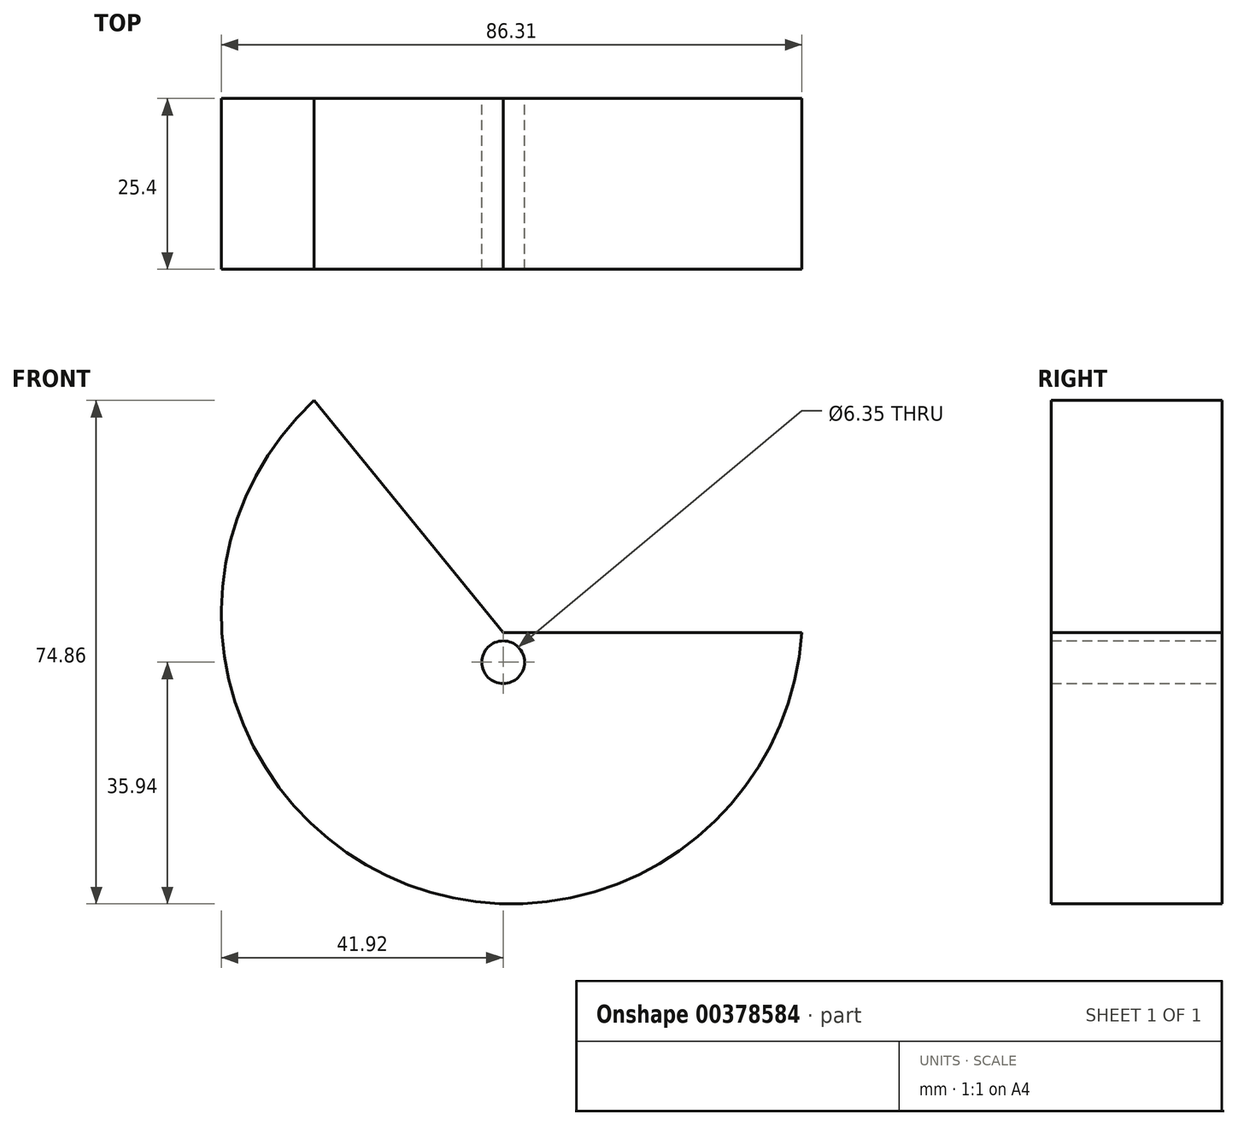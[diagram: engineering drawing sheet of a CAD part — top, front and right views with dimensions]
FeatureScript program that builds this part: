
annotation { "Feature Type Name" : "Feature", "Feature Type Description" : "" }
export const myFeature = defineFeature(function(context is Context, id is Id, definition is map)
    precondition{}
    {
        {
            var Q0;
            Q0=qCreatedBy(makeId("Front.planeOp"),FACE);
            var sketch = newSketch(context, id + "F0", { "sketchPlane" : qUnion([Q0])});
            skCircle(sketch, "E0", {"center": v(0, 0) * mm, "radius": 3.18 * mm});
            skLineSegment(sketch, "E1", {"start": v(0, 4.38) * mm, "end": v(44.39, 4.38) * mm});
            skLineSegment(sketch, "E2", {"start": v(0, 4.38) * mm, "end": v(-28.1, 38.92) * mm});
            skArc(sketch, "E3", {"start": v(-28.1, 38.92) * mm, "mid": v(-17.3, -31.74) * mm, "end": v(44.39, 4.38) * mm});
            skSolve(sketch);
        }
        {
            var Q0;
            {var subQ0=sQuery(id+"F0.wireOp",EDGE,"6a9a65d7-652e-4bca-9d3c-62b15c011ce0.27.0");var subQ1=sQuery(id+"F0.wireOp",EDGE,"dYePoZEX-iQU0-QvIu-3Huc-MhSANwJ4F8yg");var subQ2=makeQuery(id+"F0.imprint","INTERSECT",VERTEX,{"disambiguationData":[OD(0.0)],"derivedFrom":[subQ1,subQ0]});Q0=makeQuery(id+"F0.imprint","IMPRINT",FACE,{"disambiguationData":[TD([[makeQuery(id+"F0.imprint","IMPRINT",EDGE,{"disambiguationData":[TD([[subQ2,1.0]])],"derivedFrom":subQ1}),-1.0]])]});}
            var Q1;
            {var subQ0=sQuery(id+"F0.wireOp",EDGE,"6a9a65d7-652e-4bca-9d3c-62b15c011ce0.29.0");var subQ1=sQuery(id+"F0.wireOp",EDGE,"dYePoZEX-iQU0-QvIu-3Huc-MhSANwJ4F8yg");var subQ2=makeQuery(id+"F0.imprint","INTERSECT",VERTEX,{"disambiguationData":[OD(0.0)],"derivedFrom":[subQ1,subQ0]});Q1=makeQuery(id+"F0.imprint","IMPRINT",FACE,{"disambiguationData":[TD([[makeQuery(id+"F0.imprint","IMPRINT",EDGE,{"disambiguationData":[TD([[subQ2,-1.0]])],"derivedFrom":subQ1}),-1.0]])]});}
            var Q2;
            {var subQ0=sQuery(id+"F0.wireOp",EDGE,"QKdbO5Jt-CDva-Epwn-0zTl-117RtQSzYKU9");var subQ1=sQuery(id+"F0.wireOp",EDGE,"dYePoZEX-iQU0-QvIu-3Huc-MhSANwJ4F8yg");var subQ2=makeQuery(id+"F0.imprint","INTERSECT",VERTEX,{"disambiguationData":[OD(0.0)],"derivedFrom":[subQ1,subQ0]});Q2=makeQuery(id+"F0.imprint","IMPRINT",FACE,{"disambiguationData":[TD([[makeQuery(id+"F0.imprint","IMPRINT",EDGE,{"disambiguationData":[TD([[subQ2,-1.0]])],"derivedFrom":subQ1}),-1.0]])]});}
            var Q3;
            {var subQ0=sQuery(id+"F0.wireOp",EDGE,"6a9a65d7-652e-4bca-9d3c-62b15c011ce0.1.0");var subQ1=sQuery(id+"F0.wireOp",EDGE,"dYePoZEX-iQU0-QvIu-3Huc-MhSANwJ4F8yg");var subQ2=makeQuery(id+"F0.imprint","INTERSECT",VERTEX,{"disambiguationData":[OD(0.0)],"derivedFrom":[subQ1,subQ0]});Q3=makeQuery(id+"F0.imprint","IMPRINT",FACE,{"disambiguationData":[TD([[makeQuery(id+"F0.imprint","IMPRINT",EDGE,{"disambiguationData":[TD([[subQ2,-1.0]])],"derivedFrom":subQ1}),-1.0]])]});}
            var Q4;
            {var subQ0=sQuery(id+"F0.wireOp",EDGE,"6a9a65d7-652e-4bca-9d3c-62b15c011ce0.2.0");var subQ1=sQuery(id+"F0.wireOp",EDGE,"dYePoZEX-iQU0-QvIu-3Huc-MhSANwJ4F8yg");var subQ2=makeQuery(id+"F0.imprint","INTERSECT",VERTEX,{"disambiguationData":[OD(0.0)],"derivedFrom":[subQ1,subQ0]});Q4=makeQuery(id+"F0.imprint","IMPRINT",FACE,{"disambiguationData":[TD([[makeQuery(id+"F0.imprint","IMPRINT",EDGE,{"disambiguationData":[TD([[subQ2,-1.0]])],"derivedFrom":subQ1}),-1.0]])]});}
            var Q5;
            {var subQ0=sQuery(id+"F0.wireOp",EDGE,"6a9a65d7-652e-4bca-9d3c-62b15c011ce0.3.0");var subQ1=sQuery(id+"F0.wireOp",EDGE,"dYePoZEX-iQU0-QvIu-3Huc-MhSANwJ4F8yg");var subQ2=makeQuery(id+"F0.imprint","INTERSECT",VERTEX,{"disambiguationData":[OD(0.0)],"derivedFrom":[subQ1,subQ0]});Q5=makeQuery(id+"F0.imprint","IMPRINT",FACE,{"disambiguationData":[TD([[makeQuery(id+"F0.imprint","IMPRINT",EDGE,{"disambiguationData":[TD([[subQ2,-1.0]])],"derivedFrom":subQ1}),-1.0]])]});}
            var Q6;
            {var subQ0=sQuery(id+"F0.wireOp",EDGE,"6a9a65d7-652e-4bca-9d3c-62b15c011ce0.4.0");var subQ1=sQuery(id+"F0.wireOp",EDGE,"dYePoZEX-iQU0-QvIu-3Huc-MhSANwJ4F8yg");var subQ2=makeQuery(id+"F0.imprint","INTERSECT",VERTEX,{"disambiguationData":[OD(0.0)],"derivedFrom":[subQ1,subQ0]});Q6=makeQuery(id+"F0.imprint","IMPRINT",FACE,{"disambiguationData":[TD([[makeQuery(id+"F0.imprint","IMPRINT",EDGE,{"disambiguationData":[TD([[subQ2,-1.0]])],"derivedFrom":subQ1}),-1.0]])]});}
            var Q7;
            {var subQ0=sQuery(id+"F0.wireOp",EDGE,"6a9a65d7-652e-4bca-9d3c-62b15c011ce0.5.0");var subQ1=sQuery(id+"F0.wireOp",EDGE,"dYePoZEX-iQU0-QvIu-3Huc-MhSANwJ4F8yg");var subQ2=makeQuery(id+"F0.imprint","INTERSECT",VERTEX,{"disambiguationData":[OD(0.0)],"derivedFrom":[subQ1,subQ0]});Q7=makeQuery(id+"F0.imprint","IMPRINT",FACE,{"disambiguationData":[TD([[makeQuery(id+"F0.imprint","IMPRINT",EDGE,{"disambiguationData":[TD([[subQ2,-1.0]])],"derivedFrom":subQ1}),-1.0]])]});}
            var Q8;
            {var subQ0=sQuery(id+"F0.wireOp",EDGE,"6a9a65d7-652e-4bca-9d3c-62b15c011ce0.6.0");var subQ1=sQuery(id+"F0.wireOp",EDGE,"dYePoZEX-iQU0-QvIu-3Huc-MhSANwJ4F8yg");var subQ2=makeQuery(id+"F0.imprint","INTERSECT",VERTEX,{"disambiguationData":[OD(0.0)],"derivedFrom":[subQ1,subQ0]});Q8=makeQuery(id+"F0.imprint","IMPRINT",FACE,{"disambiguationData":[TD([[makeQuery(id+"F0.imprint","IMPRINT",EDGE,{"disambiguationData":[TD([[subQ2,-1.0]])],"derivedFrom":subQ1}),-1.0]])]});}
            var Q9;
            {var subQ0=sQuery(id+"F0.wireOp",EDGE,"6a9a65d7-652e-4bca-9d3c-62b15c011ce0.7.0");var subQ1=sQuery(id+"F0.wireOp",EDGE,"dYePoZEX-iQU0-QvIu-3Huc-MhSANwJ4F8yg");var subQ2=makeQuery(id+"F0.imprint","INTERSECT",VERTEX,{"disambiguationData":[OD(0.0)],"derivedFrom":[subQ1,subQ0]});Q9=makeQuery(id+"F0.imprint","IMPRINT",FACE,{"disambiguationData":[TD([[makeQuery(id+"F0.imprint","IMPRINT",EDGE,{"disambiguationData":[TD([[subQ2,-1.0]])],"derivedFrom":subQ1}),-1.0]])]});}
            var Q10;
            {var subQ0=sQuery(id+"F0.wireOp",EDGE,"6a9a65d7-652e-4bca-9d3c-62b15c011ce0.8.0");var subQ1=sQuery(id+"F0.wireOp",EDGE,"dYePoZEX-iQU0-QvIu-3Huc-MhSANwJ4F8yg");var subQ2=makeQuery(id+"F0.imprint","INTERSECT",VERTEX,{"disambiguationData":[OD(0.0)],"derivedFrom":[subQ1,subQ0]});Q10=makeQuery(id+"F0.imprint","IMPRINT",FACE,{"disambiguationData":[TD([[makeQuery(id+"F0.imprint","IMPRINT",EDGE,{"disambiguationData":[TD([[subQ2,-1.0]])],"derivedFrom":subQ1}),-1.0]])]});}
            var Q11;
            {var subQ0=sQuery(id+"F0.wireOp",EDGE,"6a9a65d7-652e-4bca-9d3c-62b15c011ce0.9.0");var subQ1=sQuery(id+"F0.wireOp",EDGE,"dYePoZEX-iQU0-QvIu-3Huc-MhSANwJ4F8yg");var subQ2=makeQuery(id+"F0.imprint","INTERSECT",VERTEX,{"disambiguationData":[OD(0.0)],"derivedFrom":[subQ1,subQ0]});Q11=makeQuery(id+"F0.imprint","IMPRINT",FACE,{"disambiguationData":[TD([[makeQuery(id+"F0.imprint","IMPRINT",EDGE,{"disambiguationData":[TD([[subQ2,-1.0]])],"derivedFrom":subQ1}),-1.0]])]});}
            var Q12;
            {var subQ0=sQuery(id+"F0.wireOp",EDGE,"6a9a65d7-652e-4bca-9d3c-62b15c011ce0.10.0");var subQ1=sQuery(id+"F0.wireOp",EDGE,"dYePoZEX-iQU0-QvIu-3Huc-MhSANwJ4F8yg");var subQ2=makeQuery(id+"F0.imprint","INTERSECT",VERTEX,{"disambiguationData":[OD(0.0)],"derivedFrom":[subQ1,subQ0]});Q12=makeQuery(id+"F0.imprint","IMPRINT",FACE,{"disambiguationData":[TD([[makeQuery(id+"F0.imprint","IMPRINT",EDGE,{"disambiguationData":[TD([[subQ2,-1.0]])],"derivedFrom":subQ1}),-1.0]])]});}
            var Q13;
            {var subQ0=sQuery(id+"F0.wireOp",EDGE,"6a9a65d7-652e-4bca-9d3c-62b15c011ce0.11.0");var subQ1=sQuery(id+"F0.wireOp",EDGE,"dYePoZEX-iQU0-QvIu-3Huc-MhSANwJ4F8yg");var subQ2=makeQuery(id+"F0.imprint","INTERSECT",VERTEX,{"disambiguationData":[OD(0.0)],"derivedFrom":[subQ1,subQ0]});Q13=makeQuery(id+"F0.imprint","IMPRINT",FACE,{"disambiguationData":[TD([[makeQuery(id+"F0.imprint","IMPRINT",EDGE,{"disambiguationData":[TD([[subQ2,-1.0]])],"derivedFrom":subQ1}),-1.0]])]});}
            var Q14;
            {var subQ0=sQuery(id+"F0.wireOp",EDGE,"6a9a65d7-652e-4bca-9d3c-62b15c011ce0.12.0");var subQ1=sQuery(id+"F0.wireOp",EDGE,"dYePoZEX-iQU0-QvIu-3Huc-MhSANwJ4F8yg");var subQ2=makeQuery(id+"F0.imprint","INTERSECT",VERTEX,{"disambiguationData":[OD(0.0)],"derivedFrom":[subQ1,subQ0]});Q14=makeQuery(id+"F0.imprint","IMPRINT",FACE,{"disambiguationData":[TD([[makeQuery(id+"F0.imprint","IMPRINT",EDGE,{"disambiguationData":[TD([[subQ2,-1.0]])],"derivedFrom":subQ1}),-1.0]])]});}
            var Q15;
            {var subQ0=sQuery(id+"F0.wireOp",EDGE,"6a9a65d7-652e-4bca-9d3c-62b15c011ce0.13.0");var subQ1=sQuery(id+"F0.wireOp",EDGE,"dYePoZEX-iQU0-QvIu-3Huc-MhSANwJ4F8yg");var subQ2=makeQuery(id+"F0.imprint","INTERSECT",VERTEX,{"disambiguationData":[OD(0.0)],"derivedFrom":[subQ1,subQ0]});Q15=makeQuery(id+"F0.imprint","IMPRINT",FACE,{"disambiguationData":[TD([[makeQuery(id+"F0.imprint","IMPRINT",EDGE,{"disambiguationData":[TD([[subQ2,-1.0]])],"derivedFrom":subQ1}),-1.0]])]});}
            var Q16;
            {var subQ0=sQuery(id+"F0.wireOp",EDGE,"6a9a65d7-652e-4bca-9d3c-62b15c011ce0.14.0");var subQ1=sQuery(id+"F0.wireOp",EDGE,"dYePoZEX-iQU0-QvIu-3Huc-MhSANwJ4F8yg");var subQ2=makeQuery(id+"F0.imprint","INTERSECT",VERTEX,{"disambiguationData":[OD(0.0)],"derivedFrom":[subQ1,subQ0]});Q16=makeQuery(id+"F0.imprint","IMPRINT",FACE,{"disambiguationData":[TD([[makeQuery(id+"F0.imprint","IMPRINT",EDGE,{"disambiguationData":[TD([[subQ2,-1.0]])],"derivedFrom":subQ1}),-1.0]])]});}
            var Q17;
            {var subQ0=sQuery(id+"F0.wireOp",EDGE,"6a9a65d7-652e-4bca-9d3c-62b15c011ce0.15.0");var subQ1=sQuery(id+"F0.wireOp",EDGE,"dYePoZEX-iQU0-QvIu-3Huc-MhSANwJ4F8yg");var subQ2=makeQuery(id+"F0.imprint","INTERSECT",VERTEX,{"disambiguationData":[OD(0.0)],"derivedFrom":[subQ1,subQ0]});Q17=makeQuery(id+"F0.imprint","IMPRINT",FACE,{"disambiguationData":[TD([[makeQuery(id+"F0.imprint","IMPRINT",EDGE,{"disambiguationData":[TD([[subQ2,-1.0]])],"derivedFrom":subQ1}),-1.0]])]});}
            var Q18;
            {var subQ0=sQuery(id+"F0.wireOp",EDGE,"6a9a65d7-652e-4bca-9d3c-62b15c011ce0.16.0");var subQ1=sQuery(id+"F0.wireOp",EDGE,"dYePoZEX-iQU0-QvIu-3Huc-MhSANwJ4F8yg");var subQ2=makeQuery(id+"F0.imprint","INTERSECT",VERTEX,{"disambiguationData":[OD(0.0)],"derivedFrom":[subQ1,subQ0]});Q18=makeQuery(id+"F0.imprint","IMPRINT",FACE,{"disambiguationData":[TD([[makeQuery(id+"F0.imprint","IMPRINT",EDGE,{"disambiguationData":[TD([[subQ2,-1.0]])],"derivedFrom":subQ1}),-1.0]])]});}
            var Q19;
            {var subQ0=sQuery(id+"F0.wireOp",EDGE,"6a9a65d7-652e-4bca-9d3c-62b15c011ce0.17.0");var subQ1=sQuery(id+"F0.wireOp",EDGE,"dYePoZEX-iQU0-QvIu-3Huc-MhSANwJ4F8yg");var subQ2=makeQuery(id+"F0.imprint","INTERSECT",VERTEX,{"disambiguationData":[OD(0.0)],"derivedFrom":[subQ1,subQ0]});Q19=makeQuery(id+"F0.imprint","IMPRINT",FACE,{"disambiguationData":[TD([[makeQuery(id+"F0.imprint","IMPRINT",EDGE,{"disambiguationData":[TD([[subQ2,-1.0]])],"derivedFrom":subQ1}),-1.0]])]});}
            var Q20;
            {var subQ0=sQuery(id+"F0.wireOp",EDGE,"6a9a65d7-652e-4bca-9d3c-62b15c011ce0.18.0");var subQ1=sQuery(id+"F0.wireOp",EDGE,"dYePoZEX-iQU0-QvIu-3Huc-MhSANwJ4F8yg");var subQ2=makeQuery(id+"F0.imprint","INTERSECT",VERTEX,{"disambiguationData":[OD(0.0)],"derivedFrom":[subQ1,subQ0]});Q20=makeQuery(id+"F0.imprint","IMPRINT",FACE,{"disambiguationData":[TD([[makeQuery(id+"F0.imprint","IMPRINT",EDGE,{"disambiguationData":[TD([[subQ2,-1.0]])],"derivedFrom":subQ1}),-1.0]])]});}
            var Q21;
            {var subQ0=sQuery(id+"F0.wireOp",EDGE,"6a9a65d7-652e-4bca-9d3c-62b15c011ce0.19.0");var subQ1=sQuery(id+"F0.wireOp",EDGE,"dYePoZEX-iQU0-QvIu-3Huc-MhSANwJ4F8yg");var subQ2=makeQuery(id+"F0.imprint","INTERSECT",VERTEX,{"disambiguationData":[OD(0.0)],"derivedFrom":[subQ1,subQ0]});Q21=makeQuery(id+"F0.imprint","IMPRINT",FACE,{"disambiguationData":[TD([[makeQuery(id+"F0.imprint","IMPRINT",EDGE,{"disambiguationData":[TD([[subQ2,-1.0]])],"derivedFrom":subQ1}),-1.0]])]});}
            var Q22;
            {var subQ0=sQuery(id+"F0.wireOp",EDGE,"6a9a65d7-652e-4bca-9d3c-62b15c011ce0.20.0");var subQ1=sQuery(id+"F0.wireOp",EDGE,"dYePoZEX-iQU0-QvIu-3Huc-MhSANwJ4F8yg");var subQ2=makeQuery(id+"F0.imprint","INTERSECT",VERTEX,{"disambiguationData":[OD(0.0)],"derivedFrom":[subQ1,subQ0]});Q22=makeQuery(id+"F0.imprint","IMPRINT",FACE,{"disambiguationData":[TD([[makeQuery(id+"F0.imprint","IMPRINT",EDGE,{"disambiguationData":[TD([[subQ2,-1.0]])],"derivedFrom":subQ1}),-1.0]])]});}
            var Q23;
            {var subQ0=sQuery(id+"F0.wireOp",EDGE,"6a9a65d7-652e-4bca-9d3c-62b15c011ce0.21.0");var subQ1=sQuery(id+"F0.wireOp",EDGE,"dYePoZEX-iQU0-QvIu-3Huc-MhSANwJ4F8yg");var subQ2=makeQuery(id+"F0.imprint","INTERSECT",VERTEX,{"disambiguationData":[OD(0.0)],"derivedFrom":[subQ1,subQ0]});Q23=makeQuery(id+"F0.imprint","IMPRINT",FACE,{"disambiguationData":[TD([[makeQuery(id+"F0.imprint","IMPRINT",EDGE,{"disambiguationData":[TD([[subQ2,-1.0]])],"derivedFrom":subQ1}),-1.0]])]});}
            var Q24;
            {var subQ0=sQuery(id+"F0.wireOp",EDGE,"6a9a65d7-652e-4bca-9d3c-62b15c011ce0.22.0");var subQ1=sQuery(id+"F0.wireOp",EDGE,"dYePoZEX-iQU0-QvIu-3Huc-MhSANwJ4F8yg");var subQ2=makeQuery(id+"F0.imprint","INTERSECT",VERTEX,{"disambiguationData":[OD(0.0)],"derivedFrom":[subQ1,subQ0]});Q24=makeQuery(id+"F0.imprint","IMPRINT",FACE,{"disambiguationData":[TD([[makeQuery(id+"F0.imprint","IMPRINT",EDGE,{"disambiguationData":[TD([[subQ2,-1.0]])],"derivedFrom":subQ1}),-1.0]])]});}
            var Q25;
            {var subQ0=sQuery(id+"F0.wireOp",EDGE,"6a9a65d7-652e-4bca-9d3c-62b15c011ce0.23.0");var subQ1=sQuery(id+"F0.wireOp",EDGE,"dYePoZEX-iQU0-QvIu-3Huc-MhSANwJ4F8yg");var subQ2=makeQuery(id+"F0.imprint","INTERSECT",VERTEX,{"disambiguationData":[OD(0.0)],"derivedFrom":[subQ1,subQ0]});Q25=makeQuery(id+"F0.imprint","IMPRINT",FACE,{"disambiguationData":[TD([[makeQuery(id+"F0.imprint","IMPRINT",EDGE,{"disambiguationData":[TD([[subQ2,-1.0]])],"derivedFrom":subQ1}),-1.0]])]});}
            var Q26;
            {var subQ0=sQuery(id+"F0.wireOp",EDGE,"6a9a65d7-652e-4bca-9d3c-62b15c011ce0.24.0");var subQ1=sQuery(id+"F0.wireOp",EDGE,"dYePoZEX-iQU0-QvIu-3Huc-MhSANwJ4F8yg");var subQ2=makeQuery(id+"F0.imprint","INTERSECT",VERTEX,{"disambiguationData":[OD(0.0)],"derivedFrom":[subQ1,subQ0]});Q26=makeQuery(id+"F0.imprint","IMPRINT",FACE,{"disambiguationData":[TD([[makeQuery(id+"F0.imprint","IMPRINT",EDGE,{"disambiguationData":[TD([[subQ2,-1.0]])],"derivedFrom":subQ1}),-1.0]])]});}
            var Q27;
            {var subQ0=sQuery(id+"F0.wireOp",EDGE,"6a9a65d7-652e-4bca-9d3c-62b15c011ce0.25.0");var subQ1=sQuery(id+"F0.wireOp",EDGE,"dYePoZEX-iQU0-QvIu-3Huc-MhSANwJ4F8yg");var subQ2=makeQuery(id+"F0.imprint","INTERSECT",VERTEX,{"disambiguationData":[OD(0.0)],"derivedFrom":[subQ1,subQ0]});Q27=makeQuery(id+"F0.imprint","IMPRINT",FACE,{"disambiguationData":[TD([[makeQuery(id+"F0.imprint","IMPRINT",EDGE,{"disambiguationData":[TD([[subQ2,-1.0]])],"derivedFrom":subQ1}),-1.0]])]});}
            var Q28;
            {var subQ0=sQuery(id+"F0.wireOp",EDGE,"6a9a65d7-652e-4bca-9d3c-62b15c011ce0.26.0");var subQ1=sQuery(id+"F0.wireOp",EDGE,"dYePoZEX-iQU0-QvIu-3Huc-MhSANwJ4F8yg");var subQ2=makeQuery(id+"F0.imprint","INTERSECT",VERTEX,{"disambiguationData":[OD(0.0)],"derivedFrom":[subQ1,subQ0]});Q28=makeQuery(id+"F0.imprint","IMPRINT",FACE,{"disambiguationData":[TD([[makeQuery(id+"F0.imprint","IMPRINT",EDGE,{"disambiguationData":[TD([[subQ2,-1.0]])],"derivedFrom":subQ1}),-1.0]])]});}
            var Q29;
            {var subQ0=sQuery(id+"F0.wireOp",EDGE,"6a9a65d7-652e-4bca-9d3c-62b15c011ce0.27.0");var subQ1=sQuery(id+"F0.wireOp",EDGE,"dYePoZEX-iQU0-QvIu-3Huc-MhSANwJ4F8yg");var subQ2=makeQuery(id+"F0.imprint","INTERSECT",VERTEX,{"disambiguationData":[OD(1.0)],"derivedFrom":[subQ1,subQ0]});Q29=makeQuery(id+"F0.imprint","IMPRINT",FACE,{"disambiguationData":[TD([[makeQuery(id+"F0.imprint","IMPRINT",EDGE,{"disambiguationData":[TD([[subQ2,-1.0]])],"derivedFrom":subQ1}),-1.0]])]});}
            var Q30;
            Q30=makeQuery(id+"F0.imprint","IMPRINT",FACE,{"disambiguationData":[TD([[makeQuery(id+"F0.imprint","IMPRINT",EDGE,{"derivedFrom":sQuery(id+"F0.wireOp",EDGE,"E0")}),-1.0]])]});
            var Q31;
            {var subQ0=sQuery(id+"F0.wireOp",EDGE,"6a9a65d7-652e-4bca-9d3c-62b15c011ce0.27.0");var subQ1=sQuery(id+"F0.wireOp",EDGE,"dYePoZEX-iQU0-QvIu-3Huc-MhSANwJ4F8yg");var subQ2=makeQuery(id+"F0.imprint","INTERSECT",VERTEX,{"disambiguationData":[OD(0.0)],"derivedFrom":[subQ1,subQ0]});Q31=makeQuery(id+"F0.imprint","IMPRINT",FACE,{"disambiguationData":[TD([[makeQuery(id+"F0.imprint","IMPRINT",EDGE,{"disambiguationData":[TD([[subQ2,-1.0]])],"derivedFrom":subQ1}),1.0]])]});}
            var Q32;
            {var subQ0=sQuery(id+"F0.wireOp",EDGE,"6a9a65d7-652e-4bca-9d3c-62b15c011ce0.28.0");var subQ1=sQuery(id+"F0.wireOp",EDGE,"dYePoZEX-iQU0-QvIu-3Huc-MhSANwJ4F8yg");var subQ2=makeQuery(id+"F0.imprint","INTERSECT",VERTEX,{"disambiguationData":[OD(1.0)],"derivedFrom":[subQ1,subQ0]});Q32=makeQuery(id+"F0.imprint","IMPRINT",FACE,{"disambiguationData":[TD([[makeQuery(id+"F0.imprint","IMPRINT",EDGE,{"disambiguationData":[TD([[subQ2,-1.0]])],"derivedFrom":subQ1}),1.0]])]});}
            var Q33;
            {var subQ0=sQuery(id+"F0.wireOp",EDGE,"6a9a65d7-652e-4bca-9d3c-62b15c011ce0.29.0");var subQ1=sQuery(id+"F0.wireOp",EDGE,"dYePoZEX-iQU0-QvIu-3Huc-MhSANwJ4F8yg");var subQ2=makeQuery(id+"F0.imprint","INTERSECT",VERTEX,{"disambiguationData":[OD(1.0)],"derivedFrom":[subQ1,subQ0]});Q33=makeQuery(id+"F0.imprint","IMPRINT",FACE,{"disambiguationData":[TD([[makeQuery(id+"F0.imprint","IMPRINT",EDGE,{"disambiguationData":[TD([[subQ2,-1.0]])],"derivedFrom":subQ1}),1.0]])]});}
            var Q34;
            {var subQ0=sQuery(id+"F0.wireOp",EDGE,"QKdbO5Jt-CDva-Epwn-0zTl-117RtQSzYKU9");var subQ1=sQuery(id+"F0.wireOp",EDGE,"dYePoZEX-iQU0-QvIu-3Huc-MhSANwJ4F8yg");var subQ2=makeQuery(id+"F0.imprint","INTERSECT",VERTEX,{"disambiguationData":[OD(1.0)],"derivedFrom":[subQ1,subQ0]});Q34=makeQuery(id+"F0.imprint","IMPRINT",FACE,{"disambiguationData":[TD([[makeQuery(id+"F0.imprint","IMPRINT",EDGE,{"disambiguationData":[TD([[subQ2,-1.0]])],"derivedFrom":subQ1}),1.0]])]});}
            var Q35;
            {var subQ0=sQuery(id+"F0.wireOp",EDGE,"6a9a65d7-652e-4bca-9d3c-62b15c011ce0.1.0");var subQ1=sQuery(id+"F0.wireOp",EDGE,"dYePoZEX-iQU0-QvIu-3Huc-MhSANwJ4F8yg");var subQ2=makeQuery(id+"F0.imprint","INTERSECT",VERTEX,{"disambiguationData":[OD(1.0)],"derivedFrom":[subQ1,subQ0]});Q35=makeQuery(id+"F0.imprint","IMPRINT",FACE,{"disambiguationData":[TD([[makeQuery(id+"F0.imprint","IMPRINT",EDGE,{"disambiguationData":[TD([[subQ2,-1.0]])],"derivedFrom":subQ1}),1.0]])]});}
            var Q36;
            {var subQ0=sQuery(id+"F0.wireOp",EDGE,"6a9a65d7-652e-4bca-9d3c-62b15c011ce0.2.0");var subQ1=sQuery(id+"F0.wireOp",EDGE,"dYePoZEX-iQU0-QvIu-3Huc-MhSANwJ4F8yg");var subQ2=makeQuery(id+"F0.imprint","INTERSECT",VERTEX,{"disambiguationData":[OD(1.0)],"derivedFrom":[subQ1,subQ0]});Q36=makeQuery(id+"F0.imprint","IMPRINT",FACE,{"disambiguationData":[TD([[makeQuery(id+"F0.imprint","IMPRINT",EDGE,{"disambiguationData":[TD([[subQ2,-1.0]])],"derivedFrom":subQ1}),1.0]])]});}
            var Q37;
            {var subQ0=sQuery(id+"F0.wireOp",EDGE,"6a9a65d7-652e-4bca-9d3c-62b15c011ce0.3.0");var subQ1=sQuery(id+"F0.wireOp",EDGE,"dYePoZEX-iQU0-QvIu-3Huc-MhSANwJ4F8yg");var subQ2=makeQuery(id+"F0.imprint","INTERSECT",VERTEX,{"disambiguationData":[OD(1.0)],"derivedFrom":[subQ1,subQ0]});Q37=makeQuery(id+"F0.imprint","IMPRINT",FACE,{"disambiguationData":[TD([[makeQuery(id+"F0.imprint","IMPRINT",EDGE,{"disambiguationData":[TD([[subQ2,-1.0]])],"derivedFrom":subQ1}),1.0]])]});}
            var Q38;
            {var subQ0=sQuery(id+"F0.wireOp",EDGE,"6a9a65d7-652e-4bca-9d3c-62b15c011ce0.4.0");var subQ1=sQuery(id+"F0.wireOp",EDGE,"dYePoZEX-iQU0-QvIu-3Huc-MhSANwJ4F8yg");var subQ2=makeQuery(id+"F0.imprint","INTERSECT",VERTEX,{"disambiguationData":[OD(1.0)],"derivedFrom":[subQ1,subQ0]});Q38=makeQuery(id+"F0.imprint","IMPRINT",FACE,{"disambiguationData":[TD([[makeQuery(id+"F0.imprint","IMPRINT",EDGE,{"disambiguationData":[TD([[subQ2,-1.0]])],"derivedFrom":subQ1}),1.0]])]});}
            var Q39;
            {var subQ0=sQuery(id+"F0.wireOp",EDGE,"6a9a65d7-652e-4bca-9d3c-62b15c011ce0.5.0");var subQ1=sQuery(id+"F0.wireOp",EDGE,"dYePoZEX-iQU0-QvIu-3Huc-MhSANwJ4F8yg");var subQ2=makeQuery(id+"F0.imprint","INTERSECT",VERTEX,{"disambiguationData":[OD(1.0)],"derivedFrom":[subQ1,subQ0]});Q39=makeQuery(id+"F0.imprint","IMPRINT",FACE,{"disambiguationData":[TD([[makeQuery(id+"F0.imprint","IMPRINT",EDGE,{"disambiguationData":[TD([[subQ2,-1.0]])],"derivedFrom":subQ1}),1.0]])]});}
            var Q40;
            {var subQ0=sQuery(id+"F0.wireOp",EDGE,"6a9a65d7-652e-4bca-9d3c-62b15c011ce0.6.0");var subQ1=sQuery(id+"F0.wireOp",EDGE,"dYePoZEX-iQU0-QvIu-3Huc-MhSANwJ4F8yg");var subQ2=makeQuery(id+"F0.imprint","INTERSECT",VERTEX,{"disambiguationData":[OD(1.0)],"derivedFrom":[subQ1,subQ0]});Q40=makeQuery(id+"F0.imprint","IMPRINT",FACE,{"disambiguationData":[TD([[makeQuery(id+"F0.imprint","IMPRINT",EDGE,{"disambiguationData":[TD([[subQ2,-1.0]])],"derivedFrom":subQ1}),1.0]])]});}
            var Q41;
            {var subQ0=sQuery(id+"F0.wireOp",EDGE,"6a9a65d7-652e-4bca-9d3c-62b15c011ce0.7.0");var subQ1=sQuery(id+"F0.wireOp",EDGE,"dYePoZEX-iQU0-QvIu-3Huc-MhSANwJ4F8yg");var subQ2=makeQuery(id+"F0.imprint","INTERSECT",VERTEX,{"disambiguationData":[OD(1.0)],"derivedFrom":[subQ1,subQ0]});Q41=makeQuery(id+"F0.imprint","IMPRINT",FACE,{"disambiguationData":[TD([[makeQuery(id+"F0.imprint","IMPRINT",EDGE,{"disambiguationData":[TD([[subQ2,-1.0]])],"derivedFrom":subQ1}),1.0]])]});}
            var Q42;
            {var subQ0=sQuery(id+"F0.wireOp",EDGE,"6a9a65d7-652e-4bca-9d3c-62b15c011ce0.8.0");var subQ1=sQuery(id+"F0.wireOp",EDGE,"dYePoZEX-iQU0-QvIu-3Huc-MhSANwJ4F8yg");var subQ2=makeQuery(id+"F0.imprint","INTERSECT",VERTEX,{"disambiguationData":[OD(1.0)],"derivedFrom":[subQ1,subQ0]});Q42=makeQuery(id+"F0.imprint","IMPRINT",FACE,{"disambiguationData":[TD([[makeQuery(id+"F0.imprint","IMPRINT",EDGE,{"disambiguationData":[TD([[subQ2,-1.0]])],"derivedFrom":subQ1}),1.0]])]});}
            var Q43;
            {var subQ0=sQuery(id+"F0.wireOp",EDGE,"6a9a65d7-652e-4bca-9d3c-62b15c011ce0.9.0");var subQ1=sQuery(id+"F0.wireOp",EDGE,"dYePoZEX-iQU0-QvIu-3Huc-MhSANwJ4F8yg");var subQ2=makeQuery(id+"F0.imprint","INTERSECT",VERTEX,{"disambiguationData":[OD(1.0)],"derivedFrom":[subQ1,subQ0]});Q43=makeQuery(id+"F0.imprint","IMPRINT",FACE,{"disambiguationData":[TD([[makeQuery(id+"F0.imprint","IMPRINT",EDGE,{"disambiguationData":[TD([[subQ2,-1.0]])],"derivedFrom":subQ1}),1.0]])]});}
            var Q44;
            {var subQ0=sQuery(id+"F0.wireOp",EDGE,"6a9a65d7-652e-4bca-9d3c-62b15c011ce0.10.0");var subQ1=sQuery(id+"F0.wireOp",EDGE,"dYePoZEX-iQU0-QvIu-3Huc-MhSANwJ4F8yg");var subQ2=makeQuery(id+"F0.imprint","INTERSECT",VERTEX,{"disambiguationData":[OD(1.0)],"derivedFrom":[subQ1,subQ0]});Q44=makeQuery(id+"F0.imprint","IMPRINT",FACE,{"disambiguationData":[TD([[makeQuery(id+"F0.imprint","IMPRINT",EDGE,{"disambiguationData":[TD([[subQ2,-1.0]])],"derivedFrom":subQ1}),1.0]])]});}
            var Q45;
            {var subQ0=sQuery(id+"F0.wireOp",EDGE,"6a9a65d7-652e-4bca-9d3c-62b15c011ce0.11.0");var subQ1=sQuery(id+"F0.wireOp",EDGE,"dYePoZEX-iQU0-QvIu-3Huc-MhSANwJ4F8yg");var subQ2=makeQuery(id+"F0.imprint","INTERSECT",VERTEX,{"disambiguationData":[OD(1.0)],"derivedFrom":[subQ1,subQ0]});Q45=makeQuery(id+"F0.imprint","IMPRINT",FACE,{"disambiguationData":[TD([[makeQuery(id+"F0.imprint","IMPRINT",EDGE,{"disambiguationData":[TD([[subQ2,-1.0]])],"derivedFrom":subQ1}),1.0]])]});}
            var Q46;
            {var subQ0=sQuery(id+"F0.wireOp",EDGE,"6a9a65d7-652e-4bca-9d3c-62b15c011ce0.12.0");var subQ1=sQuery(id+"F0.wireOp",EDGE,"dYePoZEX-iQU0-QvIu-3Huc-MhSANwJ4F8yg");var subQ2=makeQuery(id+"F0.imprint","INTERSECT",VERTEX,{"disambiguationData":[OD(1.0)],"derivedFrom":[subQ1,subQ0]});Q46=makeQuery(id+"F0.imprint","IMPRINT",FACE,{"disambiguationData":[TD([[makeQuery(id+"F0.imprint","IMPRINT",EDGE,{"disambiguationData":[TD([[subQ2,-1.0]])],"derivedFrom":subQ1}),1.0]])]});}
            var Q47;
            {var subQ0=sQuery(id+"F0.wireOp",EDGE,"6a9a65d7-652e-4bca-9d3c-62b15c011ce0.13.0");var subQ1=sQuery(id+"F0.wireOp",EDGE,"dYePoZEX-iQU0-QvIu-3Huc-MhSANwJ4F8yg");var subQ2=makeQuery(id+"F0.imprint","INTERSECT",VERTEX,{"disambiguationData":[OD(1.0)],"derivedFrom":[subQ1,subQ0]});Q47=makeQuery(id+"F0.imprint","IMPRINT",FACE,{"disambiguationData":[TD([[makeQuery(id+"F0.imprint","IMPRINT",EDGE,{"disambiguationData":[TD([[subQ2,-1.0]])],"derivedFrom":subQ1}),1.0]])]});}
            var Q48;
            {var subQ0=sQuery(id+"F0.wireOp",EDGE,"6a9a65d7-652e-4bca-9d3c-62b15c011ce0.14.0");var subQ1=sQuery(id+"F0.wireOp",EDGE,"dYePoZEX-iQU0-QvIu-3Huc-MhSANwJ4F8yg");var subQ2=makeQuery(id+"F0.imprint","INTERSECT",VERTEX,{"disambiguationData":[OD(1.0)],"derivedFrom":[subQ1,subQ0]});Q48=makeQuery(id+"F0.imprint","IMPRINT",FACE,{"disambiguationData":[TD([[makeQuery(id+"F0.imprint","IMPRINT",EDGE,{"disambiguationData":[TD([[subQ2,-1.0]])],"derivedFrom":subQ1}),1.0]])]});}
            var Q49;
            {var subQ0=sQuery(id+"F0.wireOp",EDGE,"6a9a65d7-652e-4bca-9d3c-62b15c011ce0.15.0");var subQ1=sQuery(id+"F0.wireOp",EDGE,"dYePoZEX-iQU0-QvIu-3Huc-MhSANwJ4F8yg");var subQ2=makeQuery(id+"F0.imprint","INTERSECT",VERTEX,{"disambiguationData":[OD(1.0)],"derivedFrom":[subQ1,subQ0]});Q49=makeQuery(id+"F0.imprint","IMPRINT",FACE,{"disambiguationData":[TD([[makeQuery(id+"F0.imprint","IMPRINT",EDGE,{"disambiguationData":[TD([[subQ2,-1.0]])],"derivedFrom":subQ1}),1.0]])]});}
            var Q50;
            {var subQ0=sQuery(id+"F0.wireOp",EDGE,"6a9a65d7-652e-4bca-9d3c-62b15c011ce0.16.0");var subQ1=sQuery(id+"F0.wireOp",EDGE,"dYePoZEX-iQU0-QvIu-3Huc-MhSANwJ4F8yg");var subQ2=makeQuery(id+"F0.imprint","INTERSECT",VERTEX,{"disambiguationData":[OD(1.0)],"derivedFrom":[subQ1,subQ0]});Q50=makeQuery(id+"F0.imprint","IMPRINT",FACE,{"disambiguationData":[TD([[makeQuery(id+"F0.imprint","IMPRINT",EDGE,{"disambiguationData":[TD([[subQ2,-1.0]])],"derivedFrom":subQ1}),1.0]])]});}
            var Q51;
            {var subQ0=sQuery(id+"F0.wireOp",EDGE,"6a9a65d7-652e-4bca-9d3c-62b15c011ce0.17.0");var subQ1=sQuery(id+"F0.wireOp",EDGE,"dYePoZEX-iQU0-QvIu-3Huc-MhSANwJ4F8yg");var subQ2=makeQuery(id+"F0.imprint","INTERSECT",VERTEX,{"disambiguationData":[OD(1.0)],"derivedFrom":[subQ1,subQ0]});Q51=makeQuery(id+"F0.imprint","IMPRINT",FACE,{"disambiguationData":[TD([[makeQuery(id+"F0.imprint","IMPRINT",EDGE,{"disambiguationData":[TD([[subQ2,-1.0]])],"derivedFrom":subQ1}),1.0]])]});}
            var Q52;
            {var subQ0=sQuery(id+"F0.wireOp",EDGE,"6a9a65d7-652e-4bca-9d3c-62b15c011ce0.18.0");var subQ1=sQuery(id+"F0.wireOp",EDGE,"dYePoZEX-iQU0-QvIu-3Huc-MhSANwJ4F8yg");var subQ2=makeQuery(id+"F0.imprint","INTERSECT",VERTEX,{"disambiguationData":[OD(1.0)],"derivedFrom":[subQ1,subQ0]});Q52=makeQuery(id+"F0.imprint","IMPRINT",FACE,{"disambiguationData":[TD([[makeQuery(id+"F0.imprint","IMPRINT",EDGE,{"disambiguationData":[TD([[subQ2,-1.0]])],"derivedFrom":subQ1}),1.0]])]});}
            var Q53;
            {var subQ0=sQuery(id+"F0.wireOp",EDGE,"6a9a65d7-652e-4bca-9d3c-62b15c011ce0.19.0");var subQ1=sQuery(id+"F0.wireOp",EDGE,"dYePoZEX-iQU0-QvIu-3Huc-MhSANwJ4F8yg");var subQ2=makeQuery(id+"F0.imprint","INTERSECT",VERTEX,{"disambiguationData":[OD(1.0)],"derivedFrom":[subQ1,subQ0]});Q53=makeQuery(id+"F0.imprint","IMPRINT",FACE,{"disambiguationData":[TD([[makeQuery(id+"F0.imprint","IMPRINT",EDGE,{"disambiguationData":[TD([[subQ2,-1.0]])],"derivedFrom":subQ1}),1.0]])]});}
            var Q54;
            {var subQ0=sQuery(id+"F0.wireOp",EDGE,"6a9a65d7-652e-4bca-9d3c-62b15c011ce0.20.0");var subQ1=sQuery(id+"F0.wireOp",EDGE,"dYePoZEX-iQU0-QvIu-3Huc-MhSANwJ4F8yg");var subQ2=makeQuery(id+"F0.imprint","INTERSECT",VERTEX,{"disambiguationData":[OD(1.0)],"derivedFrom":[subQ1,subQ0]});Q54=makeQuery(id+"F0.imprint","IMPRINT",FACE,{"disambiguationData":[TD([[makeQuery(id+"F0.imprint","IMPRINT",EDGE,{"disambiguationData":[TD([[subQ2,-1.0]])],"derivedFrom":subQ1}),1.0]])]});}
            var Q55;
            {var subQ0=sQuery(id+"F0.wireOp",EDGE,"6a9a65d7-652e-4bca-9d3c-62b15c011ce0.21.0");var subQ1=sQuery(id+"F0.wireOp",EDGE,"dYePoZEX-iQU0-QvIu-3Huc-MhSANwJ4F8yg");var subQ2=makeQuery(id+"F0.imprint","INTERSECT",VERTEX,{"disambiguationData":[OD(1.0)],"derivedFrom":[subQ1,subQ0]});Q55=makeQuery(id+"F0.imprint","IMPRINT",FACE,{"disambiguationData":[TD([[makeQuery(id+"F0.imprint","IMPRINT",EDGE,{"disambiguationData":[TD([[subQ2,-1.0]])],"derivedFrom":subQ1}),1.0]])]});}
            var Q56;
            {var subQ0=sQuery(id+"F0.wireOp",EDGE,"6a9a65d7-652e-4bca-9d3c-62b15c011ce0.22.0");var subQ1=sQuery(id+"F0.wireOp",EDGE,"dYePoZEX-iQU0-QvIu-3Huc-MhSANwJ4F8yg");var subQ2=makeQuery(id+"F0.imprint","INTERSECT",VERTEX,{"disambiguationData":[OD(1.0)],"derivedFrom":[subQ1,subQ0]});Q56=makeQuery(id+"F0.imprint","IMPRINT",FACE,{"disambiguationData":[TD([[makeQuery(id+"F0.imprint","IMPRINT",EDGE,{"disambiguationData":[TD([[subQ2,-1.0]])],"derivedFrom":subQ1}),1.0]])]});}
            var Q57;
            {var subQ0=sQuery(id+"F0.wireOp",EDGE,"6a9a65d7-652e-4bca-9d3c-62b15c011ce0.23.0");var subQ1=sQuery(id+"F0.wireOp",EDGE,"dYePoZEX-iQU0-QvIu-3Huc-MhSANwJ4F8yg");var subQ2=makeQuery(id+"F0.imprint","INTERSECT",VERTEX,{"disambiguationData":[OD(1.0)],"derivedFrom":[subQ1,subQ0]});Q57=makeQuery(id+"F0.imprint","IMPRINT",FACE,{"disambiguationData":[TD([[makeQuery(id+"F0.imprint","IMPRINT",EDGE,{"disambiguationData":[TD([[subQ2,-1.0]])],"derivedFrom":subQ1}),1.0]])]});}
            var Q58;
            {var subQ0=sQuery(id+"F0.wireOp",EDGE,"6a9a65d7-652e-4bca-9d3c-62b15c011ce0.24.0");var subQ1=sQuery(id+"F0.wireOp",EDGE,"dYePoZEX-iQU0-QvIu-3Huc-MhSANwJ4F8yg");var subQ2=makeQuery(id+"F0.imprint","INTERSECT",VERTEX,{"disambiguationData":[OD(1.0)],"derivedFrom":[subQ1,subQ0]});Q58=makeQuery(id+"F0.imprint","IMPRINT",FACE,{"disambiguationData":[TD([[makeQuery(id+"F0.imprint","IMPRINT",EDGE,{"disambiguationData":[TD([[subQ2,-1.0]])],"derivedFrom":subQ1}),1.0]])]});}
            var Q59;
            {var subQ0=sQuery(id+"F0.wireOp",EDGE,"6a9a65d7-652e-4bca-9d3c-62b15c011ce0.25.0");var subQ1=sQuery(id+"F0.wireOp",EDGE,"dYePoZEX-iQU0-QvIu-3Huc-MhSANwJ4F8yg");var subQ2=makeQuery(id+"F0.imprint","INTERSECT",VERTEX,{"disambiguationData":[OD(1.0)],"derivedFrom":[subQ1,subQ0]});Q59=makeQuery(id+"F0.imprint","IMPRINT",FACE,{"disambiguationData":[TD([[makeQuery(id+"F0.imprint","IMPRINT",EDGE,{"disambiguationData":[TD([[subQ2,-1.0]])],"derivedFrom":subQ1}),1.0]])]});}
            extrude(context, id + "F1", {"entities" : qUnion([Q0, Q1, Q2, Q3, Q4, Q5, Q6, Q7, Q8, Q9, Q10, Q11, Q12, Q13, Q14, Q15, Q16, Q17, Q18, Q19, Q20, Q21, Q22, Q23, Q24, Q25, Q26, Q27, Q28, Q29, Q30, Q31, Q32, Q33, Q34, Q35, Q36, Q37, Q38, Q39, Q40, Q41, Q42, Q43, Q44, Q45, Q46, Q47, Q48, Q49, Q50, Q51, Q52, Q53, Q54, Q55, Q56, Q57, Q58, Q59]), "depth" : 25.4 * mm});
        }
    });
